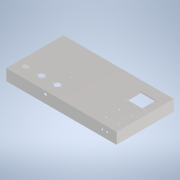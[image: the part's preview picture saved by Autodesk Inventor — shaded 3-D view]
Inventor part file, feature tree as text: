
AUTODESK INVENTOR PART (.ipt)
format: ipt  version: 2020 (Build 240168000, 168)  size: 290,304 bytes
history: native  units: mm
features: extrude x11, sketch x11
ambient origin geometry x8: Origin, YZ Plane, XZ Plane, XY Plane, X Axis, Y Axis, Z Axis, Center Point
bodies: Solid1 (feature_tree)
feature tree (22):
  extrude  "Extrusion1"  Depth=230.0mm
  extrude  "Extrusion6"  Depth=0.12mm
  extrude  "Extrusion7"  Depth=44.88mm TaperAngle=0.0deg
  extrude  "Extrusion8"  Depth=33.0mm
  extrude  "Extrusion9"  Depth=22.0mm
  extrude  "Extrusion10"  Depth=45.0mm
  extrude  "Extrusion11"  Depth=15.0mm
  extrude  "Extrusion12"  Depth=15.0mm
  extrude  "Extrusion13"  Depth=4.0mm
  extrude  "Extrusion14"  Depth=4.0mm
  extrude  "Extrusion15"  Depth=10.0mm
  sketch  "Sketch1"  dims[d0=444.0mm d1=230.0mm]
  sketch  "Sketch10"  dims[d2=45.0mm d3=0.0mm d19=0.12mm]
  sketch  "Sketch11"  dims[d20=0.12mm d21=44.88mm d22=0.0mm]
  sketch  "Sketch12"  dims[d24=22.0mm d25=33.0mm]
  sketch  "Sketch13"  dims[d27=22.0mm d30=64.0mm d31=22.0mm]
  sketch  "Sketch14"  dims[d33=64.0mm d35=45.0mm]
  sketch  "Sketch16"  dims[d36=4.0mm d37=15.0mm]
  sketch  "Sketch17"  dims[d38=4.0mm d39=15.0mm]
  sketch  "Sketch18"  dims[d40=4.0mm d41=4.0mm]
  sketch  "Sketch19"  dims[d42=4.0mm d43=4.0mm]
  sketch  "Sketch20"  dims[d44=15.0mm d45=15.0mm d46=15.0mm d47=15.0mm d50=129.25mm d52=39.45mm d54=32.4mm d55=91.7mm d56=4.0mm d57=4.0mm d58=4.0mm d59=4.0mm d60=4.0mm d61=0.0mm d65=22.5mm d66=40.65mm d67=56.0mm d68=4.2mm d69=4.2mm d70=4.2mm d71=4.2mm d72=70.5mm d73=0.0mm d74=0.0mm d75=49.7mm d77=53.4mm d79=30.5mm d80=4.2mm d81=4.2mm d82=4.2mm d83=4.2mm d84=0.0mm d85=0.0mm d86=56.0mm d87=56.0mm d88=7.1mm d89=7.1mm d90=7.1mm d92=15.0mm d94=7.1mm d95=4.0mm d96=0.0mm d97=6.0mm d98=38.0mm d100=6.0mm d101=108.95096mm d102=25.0mm d103=19.4mm d104=10.0mm d105=0.0mm d106=10.0mm d107=158.0mm d108=33.0mm d109=10.0mm d110=0.0mm d111=13.0mm d112=30.0mm d113=4.5mm d114=19.0mm d115=10.0mm d116=0.0mm d117=8.5mm d118=138.877744mm d120=72.25mm d121=8.5mm d122=24.6mm d123=13.0mm d124=10.0mm d125=0.0mm d126=52.0mm d127=17.0mm d129=17.0mm d130=200.0mm d131=4.0mm d132=4.0mm d133=5.0mm d135=10.0mm d136=0.0mm]
